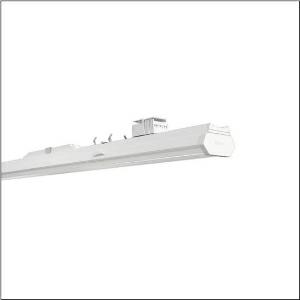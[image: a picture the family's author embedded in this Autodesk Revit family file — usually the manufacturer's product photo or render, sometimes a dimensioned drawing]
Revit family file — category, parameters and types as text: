
# Revit family: licross_r__11_protected_ho_51td12dn4fxm_db4e
name_source: partatom
category: Lighting Fixtures
units: mm (PartAtom-declared; Revit-internal decimal feet)

## family parameters
Cut with Voids When Loaded = No
Host = Face
Light Source = No
Part Type = Normal
Room Calculation Point = No
Round Connector Dimension = Use Diameter
Shared = No

## types (1)
- --- (1 x LED, 15270 lm, 87.3 W, 4000K)
    Apparent Load = 87 VA
    CIE Flux Codes = 70 91 97 98 100
    Color Rendering = 80
    Color Temperature = 4000K
    Default Elevation = 1800 mm
    Description = Licross® 11 Protected HO, luminaire insert, of sheet steel, galvanised, coil coated, white, length: 1.500mm, width: 90mm, height: 101mm, LED rated luminous flux: 15.270lm, light colour: 840, control gear: DALI 2, with plug, 5-pole, with phase selection, mains connection: 220..240V, AC, 50/60Hz, rated input power: 87W, internal wiring halogen-free, primary optical cover: cover, of PMMA, light emission: direct distribution, primary light characteristic: symmetric, protection rating (complete): IP54, insulation class (complete): insulation class I (protective earthing), certification: CE, ENEC, VDE, UKCA, protection symbol: D if used in an environment with non-conductive dust loads with corresponding accessories, impact resistance: IK06, permissible ambient temperature for indoor applications: -25..+30°C, corresponds to IFS (International Featured Standards) requirements for safety and quality in the food industry, reducing of maximum allowable ambient temperature of 5°C with ceiling mounting, LABS conformity tested according to VDMA 24364:2018-05, packaging unit: 1 piece
    Height = 92 mm
    Lamp = 1 x LED
    Lamp Light Flux = 15270 lm
    Lamp Power = 87.3 W
    Lamp count = 1
    Length = 1500 mm
    Luminous efficacy = 175 lm/W
    Manufacturer = Siteco
    ModVariant = No
    Model = 51TD12DN4FXM
    Mounting Place = Ceiling
    Mounting Type = Pendant
    Number of Poles = 1
    OnlyDefault = Yes
    Power Factor = 1
    Product Name = Licross® 11 Protected HO
    Product group = luminaire insert | ceiling pendant
    ProductGroupID = 902
    Protection Class = Protection class I
    Protection Degree = IP 54
    RLX_Detail_Level = 1
    RLX_Emergency_Light_Flux = 0 lm
    RLX_Emergency_Type = 0
    RLX_Emergency_Type_DB = No
    RlxData = <blob elided: 24473 chars, md5=ceeb692f>
    Socket = socket
    Standby Power = 0 W
    System Light Flux = 15270 lm
    System Power = 87 W
    Type Comments = factory setting: luminous flux: 100 % | dim-lin: 254 | 589 mA
    Type Image = l_1256145.jpg
    URL = http://relux.com
    VarID = @adj_122617
    Voltage = 0 V
    Weight = 0.00 kg
    Width = 88 mm

## geometry (parser evidence)
native form markers: Blend x4, Sweep x12
no freeform markers — native parametric forms only
